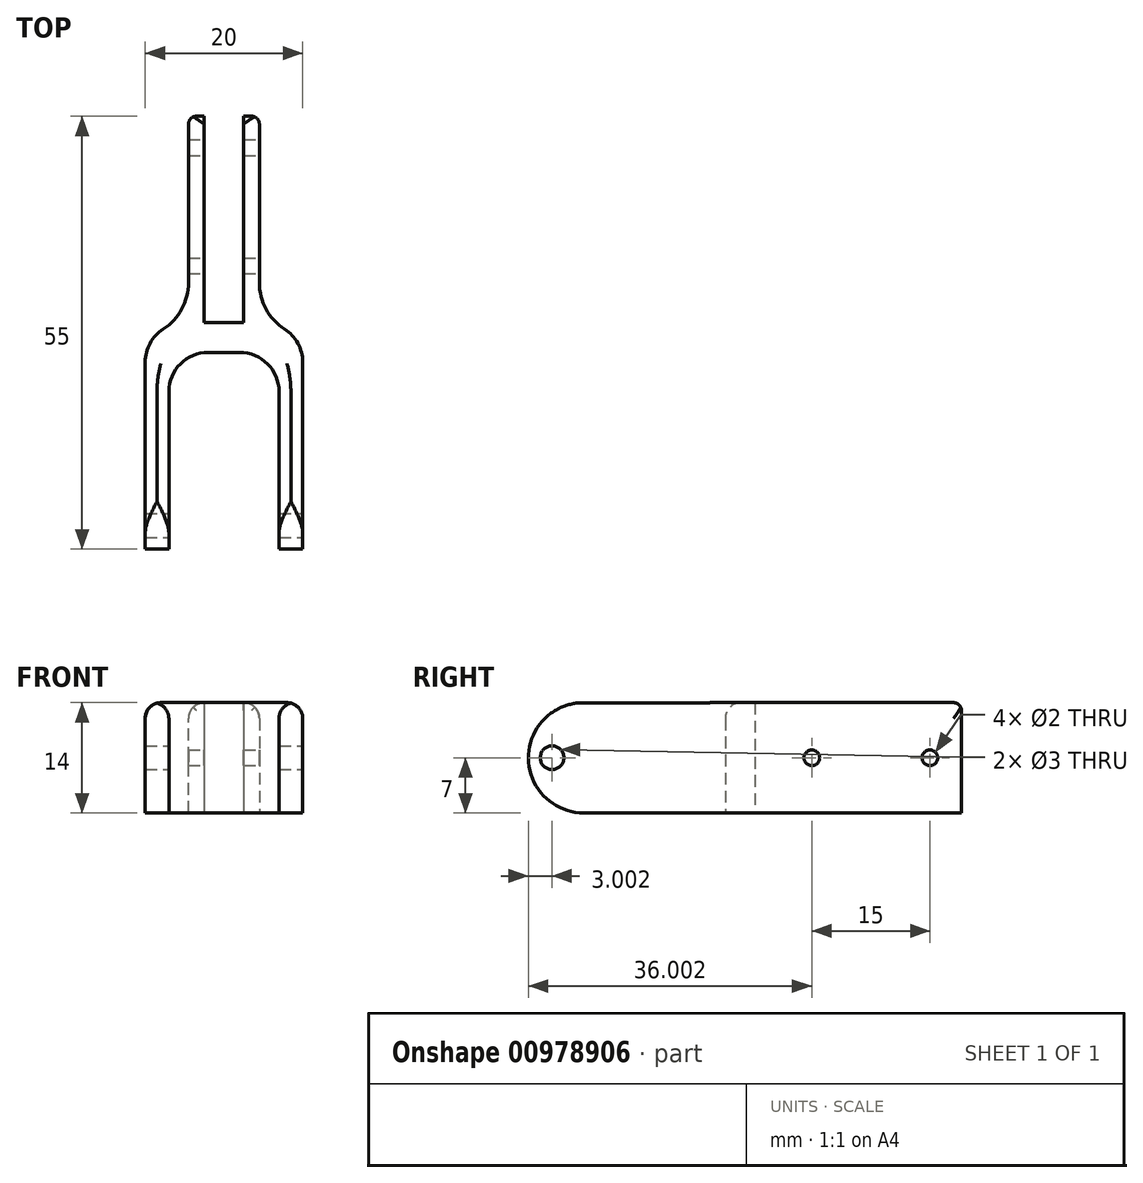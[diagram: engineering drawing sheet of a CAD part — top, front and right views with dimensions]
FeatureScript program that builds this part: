
annotation { "Feature Type Name" : "Feature", "Feature Type Description" : "" }
export const myFeature = defineFeature(function(context is Context, id is Id, definition is map)
    precondition{}
    {
        {
            var Q0;
            Q0=qCreatedBy(makeId("Top.planeOp"),FACE);
            var sketch = newSketch(context, id + "F0", { "sketchPlane" : qUnion([Q0])});
            skLineSegment(sketch, "E0", {"start": v(-14.13, 11.48) * mm, "end": v(-9.13, 11.48) * mm});
            skLineSegment(sketch, "E1", {"start": v(-9.13, 41.48) * mm, "end": v(-9.13, 11.48) * mm});
            skLineSegment(sketch, "E2", {"start": v(-14.13, 11.48) * mm, "end": v(-18.63, 11.48) * mm});
            skLineSegment(sketch, "E3", {"start": v(-18.63, -16.52) * mm, "end": v(-18.63, 11.48) * mm});
            skLineSegment(sketch, "E4", {"start": v(-9.13, 11.48) * mm, "end": v(-4.63, 11.48) * mm});
            skLineSegment(sketch, "E5", {"start": v(-4.63, 11.48) * mm, "end": v(-4.63, -16.52) * mm});
            skLineSegment(sketch, "E6", {"start": v(-14.13, 11.48) * mm, "end": v(-14.13, 41.48) * mm});
            skLineSegment(sketch, "E7.0", {"start": v(-16.13, 13.48) * mm, "end": v(-16.13, 41.48) * mm});
            skLineSegment(sketch, "E7.1", {"start": v(-16.13, 13.48) * mm, "end": v(-21.63, 13.48) * mm});
            skLineSegment(sketch, "E7.2", {"start": v(-21.63, -16.52) * mm, "end": v(-21.63, 13.48) * mm});
            skLineSegment(sketch, "E8.0", {"start": v(-1.63, 13.48) * mm, "end": v(-1.63, -16.52) * mm});
            skLineSegment(sketch, "E8.1", {"start": v(-7.13, 13.48) * mm, "end": v(-1.63, 13.48) * mm});
            skLineSegment(sketch, "E8.2", {"start": v(-7.13, 41.48) * mm, "end": v(-7.13, 13.48) * mm});
            skLineSegment(sketch, "E9", {"start": v(-16.13, 41.48) * mm, "end": v(-14.13, 41.48) * mm});
            skLineSegment(sketch, "E10", {"start": v(-9.13, 41.48) * mm, "end": v(-7.13, 41.48) * mm});
            skLineSegment(sketch, "E11", {"start": v(-21.63, -16.52) * mm, "end": v(-18.63, -16.52) * mm});
            skLineSegment(sketch, "E12", {"start": v(-4.63, -16.52) * mm, "end": v(-1.63, -16.52) * mm});
            skLineSegment(sketch, "E13", {"start": v(-14.13, 15.26) * mm, "end": v(-9.13, 15.26) * mm});
            skSolve(sketch);
        }
        {
            var Q0;
            Q0 = qSketchRegion(id + "F0", true);
            extrude(context, id + "F1", {"entities" : qUnion([Q0]), "depth" : 14 * mm, "offsetDistance" : 25 * mm});
        }
        {
            var Q0;
            Q0=makeQuery(id+"F1.opExtrude","SWEPT_FACE",FACE,{"disambiguationData":[OSD([sQuery(id+"F0.wireOp",EDGE,"E8.2")])]});
            var sketch = newSketch(context, id + "F2", { "sketchPlane" : qUnion([Q0])});
            skPoint(sketch, "E14", {"position": v(37.48, 7) * mm});
            skPoint(sketch, "E15", {"position": v(22.48, 7) * mm});
            skSolve(sketch);
        }
        {
            var Q0;
            Q0=makeQuery(id+"F1.opExtrude","SWEPT_FACE",FACE,{"disambiguationData":[OSD([sQuery(id+"F0.wireOp",EDGE,"E8.0")])]});
            var sketch = newSketch(context, id + "F3", { "sketchPlane" : qUnion([Q0])});
            skPoint(sketch, "E16", {"position": v(-10.52, 7) * mm});
            skSolve(sketch);
        }
        {
            var Q0;
            Q0=sQuery(id+"F2.wireOp",VERTEX,"E14");
            var Q1;
            Q1=sQuery(id+"F2.wireOp",VERTEX,"E15");
            var Q2;
            Q2=makeQuery(id+"F1.opExtrude","SWEPT_BODY",BODY,{"disambiguationData":[OSD([sQuery(id+"F0.wireOp",EDGE,"E0"),sQuery(id+"F0.wireOp",EDGE,"E1"),sQuery(id+"F0.wireOp",EDGE,"E2"),sQuery(id+"F0.wireOp",EDGE,"E3"),sQuery(id+"F0.wireOp",EDGE,"E4"),sQuery(id+"F0.wireOp",EDGE,"E5"),sQuery(id+"F0.wireOp",EDGE,"E6"),sQuery(id+"F0.wireOp",EDGE,"E7.0"),sQuery(id+"F0.wireOp",EDGE,"E7.1"),sQuery(id+"F0.wireOp",EDGE,"E7.2"),sQuery(id+"F0.wireOp",EDGE,"E8.0"),sQuery(id+"F0.wireOp",EDGE,"E8.1"),sQuery(id+"F0.wireOp",EDGE,"E8.2"),sQuery(id+"F0.wireOp",EDGE,"E9"),sQuery(id+"F0.wireOp",EDGE,"E10"),sQuery(id+"F0.wireOp",EDGE,"E11"),sQuery(id+"F0.wireOp",EDGE,"E12"),sQuery(id+"F0.wireOp",EDGE,"E13")])]});
            hole(context, id + "F4", {"style" : HoleStyle.SIMPLE, "endStyle" : HoleEndStyle.THROUGH, "holeDiameter" : 2 * mm, "majorDiameter" : 5 * mm, "isTappedThrough" : true, "tappedDepth" : 12 * mm, "tapClearance" : 3, "locations" : qUnion([Q0, Q1]), "scope" : qUnion([Q2])});
        }
        {
            var Q0;
            Q0=sQuery(id+"F3.wireOp",VERTEX,"E16");
            var Q1;
            Q1=makeQuery(id+"F1.opExtrude","SWEPT_BODY",BODY,{"disambiguationData":[OSD([sQuery(id+"F0.wireOp",EDGE,"E0"),sQuery(id+"F0.wireOp",EDGE,"E1"),sQuery(id+"F0.wireOp",EDGE,"E2"),sQuery(id+"F0.wireOp",EDGE,"E3"),sQuery(id+"F0.wireOp",EDGE,"E4"),sQuery(id+"F0.wireOp",EDGE,"E5"),sQuery(id+"F0.wireOp",EDGE,"E6"),sQuery(id+"F0.wireOp",EDGE,"E7.0"),sQuery(id+"F0.wireOp",EDGE,"E7.1"),sQuery(id+"F0.wireOp",EDGE,"E7.2"),sQuery(id+"F0.wireOp",EDGE,"E8.0"),sQuery(id+"F0.wireOp",EDGE,"E8.1"),sQuery(id+"F0.wireOp",EDGE,"E8.2"),sQuery(id+"F0.wireOp",EDGE,"E9"),sQuery(id+"F0.wireOp",EDGE,"E10"),sQuery(id+"F0.wireOp",EDGE,"E11"),sQuery(id+"F0.wireOp",EDGE,"E12"),sQuery(id+"F0.wireOp",EDGE,"E13")])]});
            hole(context, id + "F5", {"style" : HoleStyle.SIMPLE, "endStyle" : HoleEndStyle.THROUGH, "holeDiameter" : 3 * mm, "majorDiameter" : 5 * mm, "isTappedThrough" : true, "tappedDepth" : 12 * mm, "tapClearance" : 3, "locations" : qUnion([Q0]), "scope" : qUnion([Q1])});
        }
        {
            var Q0;
            Q0=makeQuery(id+"F1.opExtrude","SWEPT_EDGE",EDGE,{"disambiguationData":[OSD([sQuery(id+"F0.wireOp",EDGE,"E8.1"),sQuery(id+"F0.wireOp",EDGE,"E8.2")])]});
            var Q1;
            Q1=makeQuery(id+"F1.opExtrude","SWEPT_EDGE",EDGE,{"disambiguationData":[OSD([sQuery(id+"F0.wireOp",EDGE,"E7.0"),sQuery(id+"F0.wireOp",EDGE,"E7.1")])]});
            fillet(context, id + "F6", {"entities" : qUnion([Q0, Q1]), "radius" : 7 * mm, "tangentPropagation" : true, "allowEdgeOverflow" : false});
        }
        {
            var Q0;
            Q0=makeQuery(id+"F6.opFillet","BLEND_EDGE",EDGE,{"blendedFrom":[makeQuery(id+"F1.opExtrude","SWEPT_EDGE",EDGE,{"disambiguationData":[OSD([sQuery(id+"F0.wireOp",EDGE,"E7.0"),sQuery(id+"F0.wireOp",EDGE,"E7.1")])]}),makeQuery(id+"F1.opExtrude","SWEPT_FACE",FACE,{"disambiguationData":[OSD([sQuery(id+"F0.wireOp",EDGE,"E7.2")])]})],"blendedInto":[makeQuery(id+"F1.opExtrude","SWEPT_FACE",FACE,{"disambiguationData":[OSD([sQuery(id+"F0.wireOp",EDGE,"E7.2")])]})]});
            var Q1;
            Q1=makeQuery(id+"F6.opFillet","BLEND_EDGE",EDGE,{"blendedFrom":[makeQuery(id+"F1.opExtrude","SWEPT_EDGE",EDGE,{"disambiguationData":[OSD([sQuery(id+"F0.wireOp",EDGE,"E8.1"),sQuery(id+"F0.wireOp",EDGE,"E8.2")])]}),makeQuery(id+"F1.opExtrude","SWEPT_FACE",FACE,{"disambiguationData":[OSD([sQuery(id+"F0.wireOp",EDGE,"E8.0")])]})],"blendedInto":[makeQuery(id+"F1.opExtrude","SWEPT_FACE",FACE,{"disambiguationData":[OSD([sQuery(id+"F0.wireOp",EDGE,"E8.0")])]})]});
            fillet(context, id + "F7", {"entities" : qUnion([Q0, Q1]), "radius" : 5 * mm, "tangentPropagation" : true, "allowEdgeOverflow" : false});
        }
        {
            var Q0;
            Q0=makeQuery(id+"F1.opExtrude","SWEPT_EDGE",EDGE,{"disambiguationData":[OSD([sQuery(id+"F0.wireOp",EDGE,"E2"),sQuery(id+"F0.wireOp",EDGE,"E3")])]});
            var Q1;
            Q1=makeQuery(id+"F1.opExtrude","SWEPT_EDGE",EDGE,{"disambiguationData":[OSD([sQuery(id+"F0.wireOp",EDGE,"E4"),sQuery(id+"F0.wireOp",EDGE,"E5")])]});
            fillet(context, id + "F8", {"entities" : qUnion([Q0, Q1]), "radius" : 5 * mm, "tangentPropagation" : true, "allowEdgeOverflow" : false});
        }
        {
            var Q0;
            Q0=makeQuery(id+"F1.opExtrude","CAP_EDGE",EDGE,{"disambiguationData":[OSD([sQuery(id+"F0.wireOp",EDGE,"E11")])],"isStart":false});
            var Q1;
            Q1=makeQuery(id+"F1.opExtrude","CAP_EDGE",EDGE,{"disambiguationData":[OSD([sQuery(id+"F0.wireOp",EDGE,"E12")])],"isStart":false});
            fillet(context, id + "F9", {"entities" : qUnion([Q0, Q1]), "radius" : 10 * mm, "tangentPropagation" : true, "allowEdgeOverflow" : false});
        }
        {
            var Q0;
            Q0=makeQuery(id+"F1.opExtrude","CAP_EDGE",EDGE,{"disambiguationData":[OSD([sQuery(id+"F0.wireOp",EDGE,"E12")])],"isStart":true});
            var Q1;
            Q1=makeQuery(id+"F1.opExtrude","CAP_EDGE",EDGE,{"disambiguationData":[OSD([sQuery(id+"F0.wireOp",EDGE,"E11")])],"isStart":true});
            fillet(context, id + "F10", {"entities" : qUnion([Q0, Q1]), "radius" : 7 * mm, "tangentPropagation" : true, "allowEdgeOverflow" : false});
        }
        {
            var Q0;
            Q0=makeQuery(id+"F1.opExtrude","CAP_EDGE",EDGE,{"disambiguationData":[OSD([sQuery(id+"F0.wireOp",EDGE,"E9")])],"isStart":false});
            var Q1;
            Q1=makeQuery(id+"F1.opExtrude","SWEPT_EDGE",EDGE,{"disambiguationData":[OSD([sQuery(id+"F0.wireOp",EDGE,"E7.0"),sQuery(id+"F0.wireOp",EDGE,"E9")])]});
            var Q2;
            Q2=makeQuery(id+"F1.opExtrude","SWEPT_EDGE",EDGE,{"disambiguationData":[OSD([sQuery(id+"F0.wireOp",EDGE,"E8.2"),sQuery(id+"F0.wireOp",EDGE,"E10")])]});
            fillet(context, id + "F11", {"entities" : qUnion([Q0, Q1, Q2]), "radius" : 1 * mm, "tangentPropagation" : true, "allowEdgeOverflow" : false});
        }
        {
            var Q0;
            Q0=makeQuery(id+"F1.opExtrude","CAP_EDGE",EDGE,{"disambiguationData":[OSD([sQuery(id+"F0.wireOp",EDGE,"E10")])],"isStart":false});
            fillet(context, id + "F12", {"entities" : qUnion([Q0]), "radius" : 1 * mm, "allowEdgeOverflow" : false});
        }
        {
            var Q0;
            Q0=makeQuery(id+"F1.opExtrude","CAP_EDGE",EDGE,{"disambiguationData":[OSD([sQuery(id+"F0.wireOp",EDGE,"E7.0")])],"isStart":false});
            var Q1;
            Q1=makeQuery(id+"F1.opExtrude","CAP_EDGE",EDGE,{"disambiguationData":[OSD([sQuery(id+"F0.wireOp",EDGE,"E8.2")])],"isStart":false});
            var Q2;
            {var subQ0=sQuery(id+"F0.wireOp",EDGE,"E7.1");var subQ1=sQuery(id+"F0.wireOp",EDGE,"E7.0");Q2=makeQuery(id+"F6.opFillet","BLEND_EDGE",EDGE,{"blendedFrom":[makeQuery(id+"F1.opExtrude","SWEPT_EDGE",EDGE,{"disambiguationData":[OSD([subQ1,subQ0])]}),makeQuery(id+"F1.opExtrude","CAP_FACE",FACE,{"disambiguationData":[OSD([sQuery(id+"F0.wireOp",EDGE,"E0"),sQuery(id+"F0.wireOp",EDGE,"E1"),sQuery(id+"F0.wireOp",EDGE,"E2"),sQuery(id+"F0.wireOp",EDGE,"E3"),sQuery(id+"F0.wireOp",EDGE,"E4"),sQuery(id+"F0.wireOp",EDGE,"E5"),sQuery(id+"F0.wireOp",EDGE,"E6"),subQ1,subQ0,sQuery(id+"F0.wireOp",EDGE,"E7.2"),sQuery(id+"F0.wireOp",EDGE,"E8.0"),sQuery(id+"F0.wireOp",EDGE,"E8.1"),sQuery(id+"F0.wireOp",EDGE,"E8.2"),sQuery(id+"F0.wireOp",EDGE,"E9"),sQuery(id+"F0.wireOp",EDGE,"E10"),sQuery(id+"F0.wireOp",EDGE,"E11"),sQuery(id+"F0.wireOp",EDGE,"E12"),sQuery(id+"F0.wireOp",EDGE,"E13")])],"isStart":false})],"blendedInto":[makeQuery(id+"F1.opExtrude","CAP_FACE",FACE,{"disambiguationData":[OSD([sQuery(id+"F0.wireOp",EDGE,"E0"),sQuery(id+"F0.wireOp",EDGE,"E1"),sQuery(id+"F0.wireOp",EDGE,"E2"),sQuery(id+"F0.wireOp",EDGE,"E3"),sQuery(id+"F0.wireOp",EDGE,"E4"),sQuery(id+"F0.wireOp",EDGE,"E5"),sQuery(id+"F0.wireOp",EDGE,"E6"),subQ1,subQ0,sQuery(id+"F0.wireOp",EDGE,"E7.2"),sQuery(id+"F0.wireOp",EDGE,"E8.0"),sQuery(id+"F0.wireOp",EDGE,"E8.1"),sQuery(id+"F0.wireOp",EDGE,"E8.2"),sQuery(id+"F0.wireOp",EDGE,"E9"),sQuery(id+"F0.wireOp",EDGE,"E10"),sQuery(id+"F0.wireOp",EDGE,"E11"),sQuery(id+"F0.wireOp",EDGE,"E12"),sQuery(id+"F0.wireOp",EDGE,"E13")])],"isStart":false})]});}
            var Q3;
            {var subQ0=sQuery(id+"F0.wireOp",EDGE,"E8.2");var subQ1=sQuery(id+"F0.wireOp",EDGE,"E8.1");Q3=makeQuery(id+"F6.opFillet","BLEND_EDGE",EDGE,{"blendedFrom":[makeQuery(id+"F1.opExtrude","SWEPT_EDGE",EDGE,{"disambiguationData":[OSD([subQ1,subQ0])]}),makeQuery(id+"F1.opExtrude","CAP_FACE",FACE,{"disambiguationData":[OSD([sQuery(id+"F0.wireOp",EDGE,"E0"),sQuery(id+"F0.wireOp",EDGE,"E1"),sQuery(id+"F0.wireOp",EDGE,"E2"),sQuery(id+"F0.wireOp",EDGE,"E3"),sQuery(id+"F0.wireOp",EDGE,"E4"),sQuery(id+"F0.wireOp",EDGE,"E5"),sQuery(id+"F0.wireOp",EDGE,"E6"),sQuery(id+"F0.wireOp",EDGE,"E7.0"),sQuery(id+"F0.wireOp",EDGE,"E7.1"),sQuery(id+"F0.wireOp",EDGE,"E7.2"),sQuery(id+"F0.wireOp",EDGE,"E8.0"),subQ1,subQ0,sQuery(id+"F0.wireOp",EDGE,"E9"),sQuery(id+"F0.wireOp",EDGE,"E10"),sQuery(id+"F0.wireOp",EDGE,"E11"),sQuery(id+"F0.wireOp",EDGE,"E12"),sQuery(id+"F0.wireOp",EDGE,"E13")])],"isStart":false})],"blendedInto":[makeQuery(id+"F1.opExtrude","CAP_FACE",FACE,{"disambiguationData":[OSD([sQuery(id+"F0.wireOp",EDGE,"E0"),sQuery(id+"F0.wireOp",EDGE,"E1"),sQuery(id+"F0.wireOp",EDGE,"E2"),sQuery(id+"F0.wireOp",EDGE,"E3"),sQuery(id+"F0.wireOp",EDGE,"E4"),sQuery(id+"F0.wireOp",EDGE,"E5"),sQuery(id+"F0.wireOp",EDGE,"E6"),sQuery(id+"F0.wireOp",EDGE,"E7.0"),sQuery(id+"F0.wireOp",EDGE,"E7.1"),sQuery(id+"F0.wireOp",EDGE,"E7.2"),sQuery(id+"F0.wireOp",EDGE,"E8.0"),subQ1,subQ0,sQuery(id+"F0.wireOp",EDGE,"E9"),sQuery(id+"F0.wireOp",EDGE,"E10"),sQuery(id+"F0.wireOp",EDGE,"E11"),sQuery(id+"F0.wireOp",EDGE,"E12"),sQuery(id+"F0.wireOp",EDGE,"E13")])],"isStart":false})]});}
            var Q4;
            {var subQ0=sQuery(id+"F0.wireOp",EDGE,"E7.2");var subQ1=sQuery(id+"F0.wireOp",EDGE,"E7.1");var subQ2=sQuery(id+"F0.wireOp",EDGE,"E7.0");Q4=makeQuery(id+"F7.opFillet","BLEND_EDGE",EDGE,{"blendedFrom":[makeQuery(id+"F6.opFillet","BLEND_EDGE",EDGE,{"blendedFrom":[makeQuery(id+"F1.opExtrude","SWEPT_EDGE",EDGE,{"disambiguationData":[OSD([subQ2,subQ1])]}),makeQuery(id+"F1.opExtrude","SWEPT_FACE",FACE,{"disambiguationData":[OSD([subQ0])]})],"blendedInto":[makeQuery(id+"F1.opExtrude","SWEPT_FACE",FACE,{"disambiguationData":[OSD([subQ0])]})]}),makeQuery(id+"F1.opExtrude","CAP_FACE",FACE,{"disambiguationData":[OSD([sQuery(id+"F0.wireOp",EDGE,"E0"),sQuery(id+"F0.wireOp",EDGE,"E1"),sQuery(id+"F0.wireOp",EDGE,"E2"),sQuery(id+"F0.wireOp",EDGE,"E3"),sQuery(id+"F0.wireOp",EDGE,"E4"),sQuery(id+"F0.wireOp",EDGE,"E5"),sQuery(id+"F0.wireOp",EDGE,"E6"),subQ2,subQ1,subQ0,sQuery(id+"F0.wireOp",EDGE,"E8.0"),sQuery(id+"F0.wireOp",EDGE,"E8.1"),sQuery(id+"F0.wireOp",EDGE,"E8.2"),sQuery(id+"F0.wireOp",EDGE,"E9"),sQuery(id+"F0.wireOp",EDGE,"E10"),sQuery(id+"F0.wireOp",EDGE,"E11"),sQuery(id+"F0.wireOp",EDGE,"E12"),sQuery(id+"F0.wireOp",EDGE,"E13")])],"isStart":false})],"blendedInto":[makeQuery(id+"F1.opExtrude","CAP_FACE",FACE,{"disambiguationData":[OSD([sQuery(id+"F0.wireOp",EDGE,"E0"),sQuery(id+"F0.wireOp",EDGE,"E1"),sQuery(id+"F0.wireOp",EDGE,"E2"),sQuery(id+"F0.wireOp",EDGE,"E3"),sQuery(id+"F0.wireOp",EDGE,"E4"),sQuery(id+"F0.wireOp",EDGE,"E5"),sQuery(id+"F0.wireOp",EDGE,"E6"),subQ2,subQ1,subQ0,sQuery(id+"F0.wireOp",EDGE,"E8.0"),sQuery(id+"F0.wireOp",EDGE,"E8.1"),sQuery(id+"F0.wireOp",EDGE,"E8.2"),sQuery(id+"F0.wireOp",EDGE,"E9"),sQuery(id+"F0.wireOp",EDGE,"E10"),sQuery(id+"F0.wireOp",EDGE,"E11"),sQuery(id+"F0.wireOp",EDGE,"E12"),sQuery(id+"F0.wireOp",EDGE,"E13")])],"isStart":false})]});}
            var Q5;
            Q5=makeQuery(id+"F1.opExtrude","CAP_EDGE",EDGE,{"disambiguationData":[OSD([sQuery(id+"F0.wireOp",EDGE,"E7.2")])],"isStart":false});
            var Q6;
            Q6=makeQuery(id+"F1.opExtrude","CAP_EDGE",EDGE,{"disambiguationData":[OSD([sQuery(id+"F0.wireOp",EDGE,"E8.0")])],"isStart":false});
            var Q7;
            {var subQ0=sQuery(id+"F0.wireOp",EDGE,"E3");var subQ1=sQuery(id+"F0.wireOp",EDGE,"E2");Q7=makeQuery(id+"F8.opFillet","BLEND_EDGE",EDGE,{"blendedFrom":[makeQuery(id+"F1.opExtrude","SWEPT_EDGE",EDGE,{"disambiguationData":[OSD([subQ1,subQ0])]}),makeQuery(id+"F1.opExtrude","CAP_FACE",FACE,{"disambiguationData":[OSD([sQuery(id+"F0.wireOp",EDGE,"E0"),sQuery(id+"F0.wireOp",EDGE,"E1"),subQ1,subQ0,sQuery(id+"F0.wireOp",EDGE,"E4"),sQuery(id+"F0.wireOp",EDGE,"E5"),sQuery(id+"F0.wireOp",EDGE,"E6"),sQuery(id+"F0.wireOp",EDGE,"E7.0"),sQuery(id+"F0.wireOp",EDGE,"E7.1"),sQuery(id+"F0.wireOp",EDGE,"E7.2"),sQuery(id+"F0.wireOp",EDGE,"E8.0"),sQuery(id+"F0.wireOp",EDGE,"E8.1"),sQuery(id+"F0.wireOp",EDGE,"E8.2"),sQuery(id+"F0.wireOp",EDGE,"E9"),sQuery(id+"F0.wireOp",EDGE,"E10"),sQuery(id+"F0.wireOp",EDGE,"E11"),sQuery(id+"F0.wireOp",EDGE,"E12"),sQuery(id+"F0.wireOp",EDGE,"E13")])],"isStart":false})],"blendedInto":[makeQuery(id+"F1.opExtrude","CAP_FACE",FACE,{"disambiguationData":[OSD([sQuery(id+"F0.wireOp",EDGE,"E0"),sQuery(id+"F0.wireOp",EDGE,"E1"),subQ1,subQ0,sQuery(id+"F0.wireOp",EDGE,"E4"),sQuery(id+"F0.wireOp",EDGE,"E5"),sQuery(id+"F0.wireOp",EDGE,"E6"),sQuery(id+"F0.wireOp",EDGE,"E7.0"),sQuery(id+"F0.wireOp",EDGE,"E7.1"),sQuery(id+"F0.wireOp",EDGE,"E7.2"),sQuery(id+"F0.wireOp",EDGE,"E8.0"),sQuery(id+"F0.wireOp",EDGE,"E8.1"),sQuery(id+"F0.wireOp",EDGE,"E8.2"),sQuery(id+"F0.wireOp",EDGE,"E9"),sQuery(id+"F0.wireOp",EDGE,"E10"),sQuery(id+"F0.wireOp",EDGE,"E11"),sQuery(id+"F0.wireOp",EDGE,"E12"),sQuery(id+"F0.wireOp",EDGE,"E13")])],"isStart":false})]});}
            var Q8;
            Q8=makeQuery(id+"F1.opExtrude","CAP_EDGE",EDGE,{"disambiguationData":[OSD([sQuery(id+"F0.wireOp",EDGE,"E0"),sQuery(id+"F0.wireOp",EDGE,"E2"),sQuery(id+"F0.wireOp",EDGE,"E4")])],"isStart":false});
            var Q9;
            Q9=makeQuery(id+"F1.opExtrude","CAP_EDGE",EDGE,{"disambiguationData":[OSD([sQuery(id+"F0.wireOp",EDGE,"E3")])],"isStart":false});
            fillet(context, id + "F13", {"entities" : qUnion([Q0, Q1, Q2, Q3, Q4, Q5, Q6, Q7, Q8, Q9]), "radius" : 2 * mm, "allowEdgeOverflow" : false});
        }
    });
